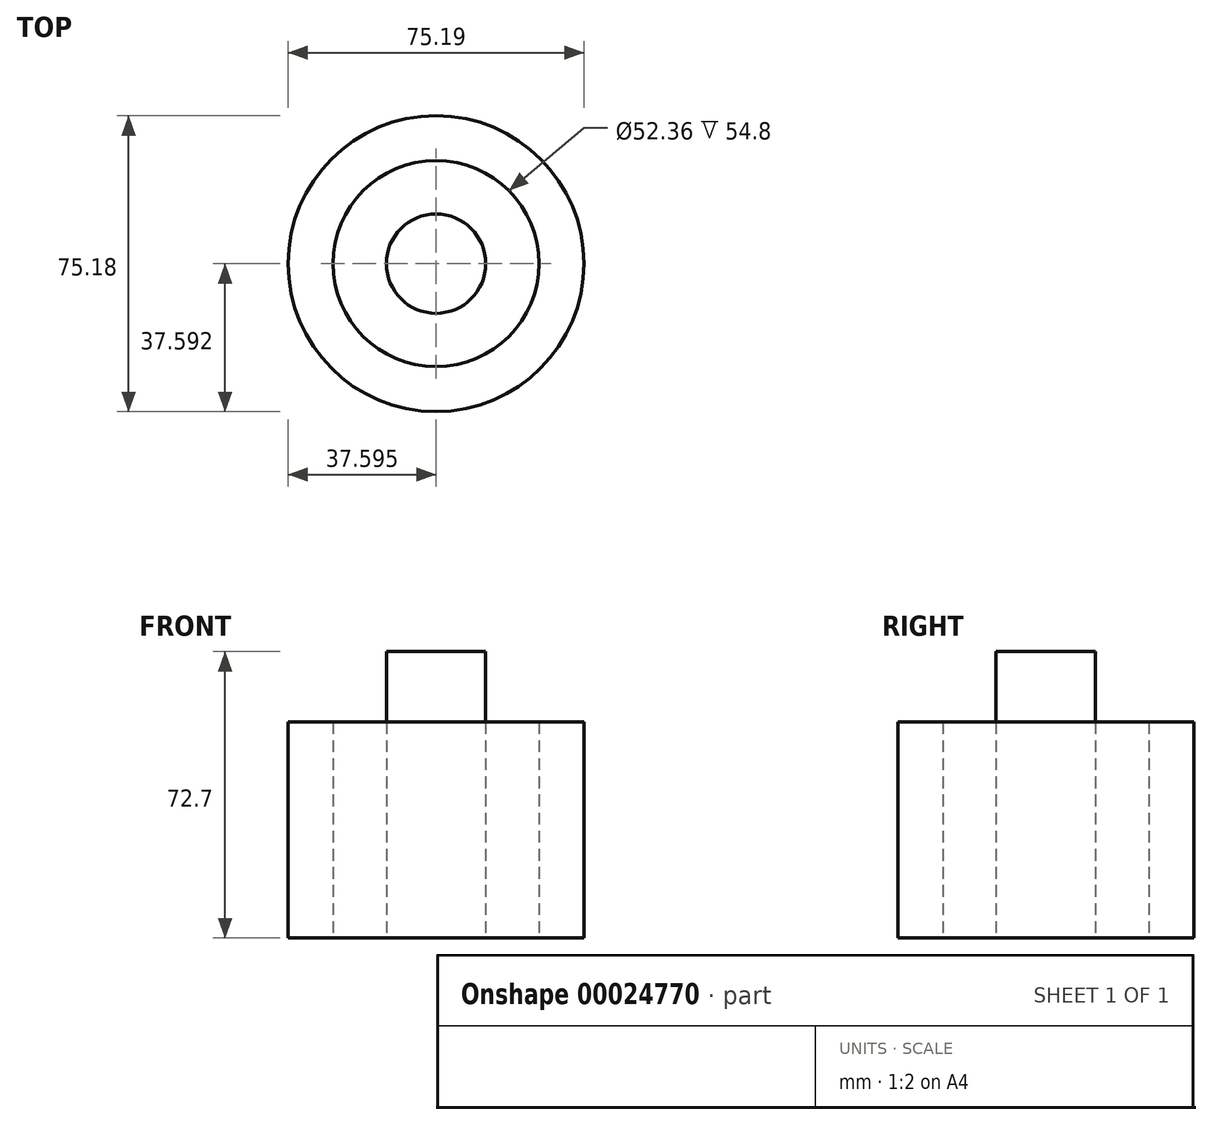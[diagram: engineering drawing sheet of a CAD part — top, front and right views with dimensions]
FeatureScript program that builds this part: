
annotation { "Feature Type Name" : "Feature", "Feature Type Description" : "" }
export const myFeature = defineFeature(function(context is Context, id is Id, definition is map)
    precondition{}
    {
        {
            var Q0;
            Q0=qCreatedBy(makeId("Top.planeOp"),FACE);
            var sketch = newSketch(context, id + "F0", { "sketchPlane" : qUnion([Q0])});
            skCircle(sketch, "E0", {"center": v(-30.46, 8.7) * mm, "radius": 37.6 * mm});
            skCircle(sketch, "E1", {"center": v(-30.46, 8.7) * mm, "radius": 26.18 * mm});
            skCircle(sketch, "E2", {"center": v(-30.46, 8.7) * mm, "radius": 12.62 * mm});
            skSolve(sketch);
        }
        {
            var Q0;
            Q0 = qSketchRegion(id + "F0", true);
            var Q1;
            Q1=makeQuery(id+"F0.imprint","IMPRINT",FACE,{"disambiguationData":[TD([[makeQuery(id+"F0.imprint","IMPRINT",EDGE,{"derivedFrom":sQuery(id+"F0.wireOp",EDGE,"E2")}),1.0]])]});
            extrude(context, id + "F1", {"entities" : qUnion([Q0, Q1]), "depth" : 54.8 * mm});
        }
        {
            var Q0;
            Q0=makeQuery(id+"F1.opExtrude","CAP_FACE",FACE,{"disambiguationData":[OSD([sQuery(id+"F0.wireOp",EDGE,"E2")])],"isStart":false});
            extrude(context, id + "F2", {"entities" : qUnion([Q0]), "operationType" : NewBodyOperationType.ADD, "depth" : 17.9 * mm});
        }
    });
